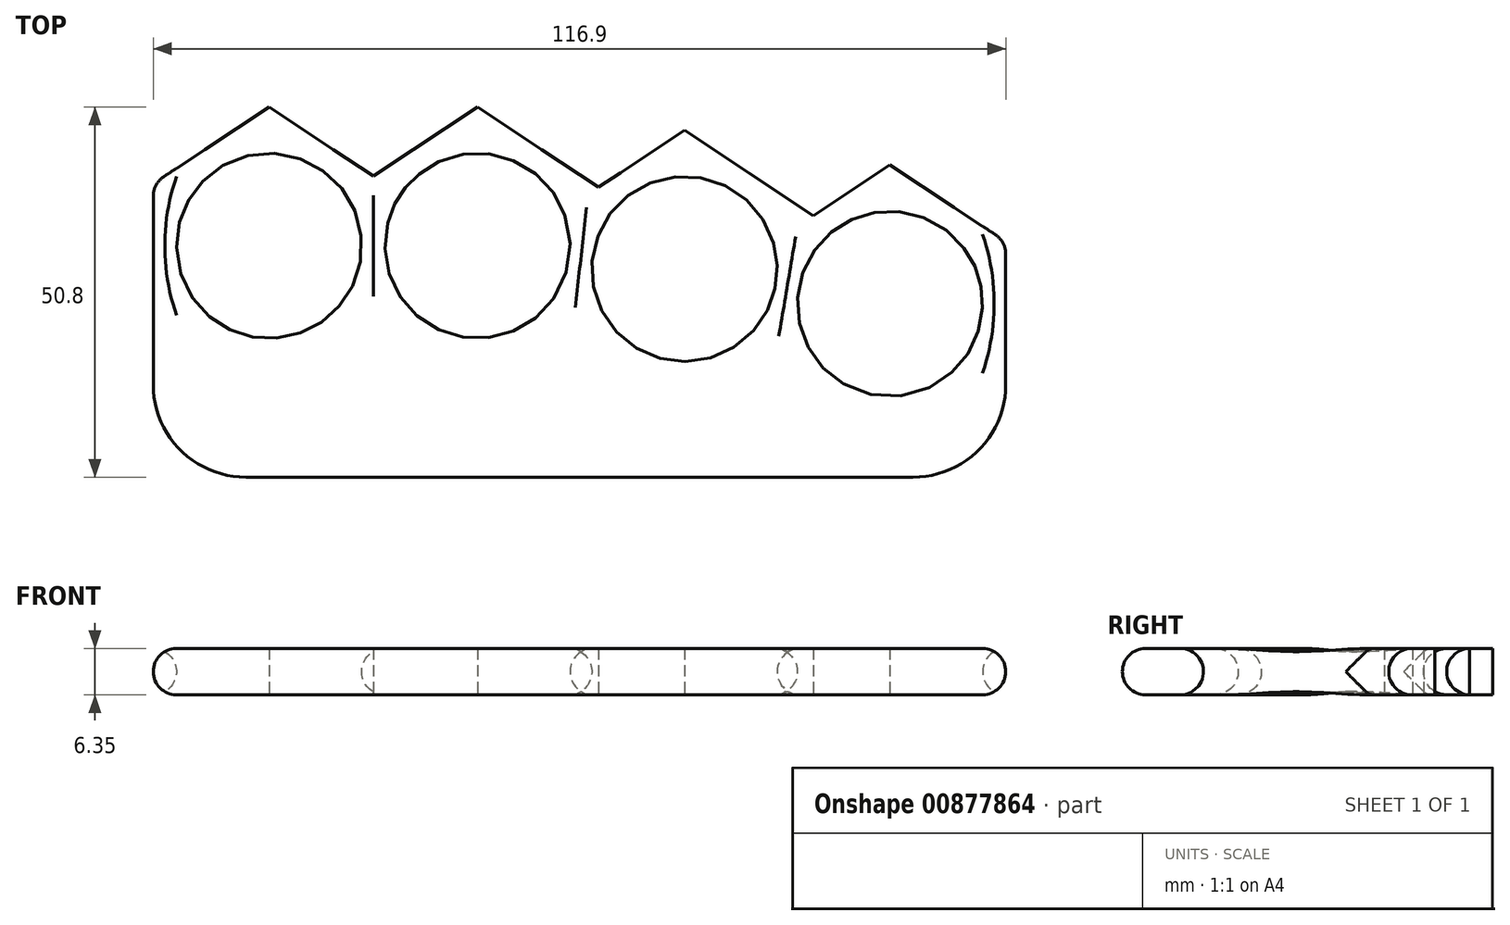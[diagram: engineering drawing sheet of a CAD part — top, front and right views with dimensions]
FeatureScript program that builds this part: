
annotation { "Feature Type Name" : "Feature", "Feature Type Description" : "" }
export const myFeature = defineFeature(function(context is Context, id is Id, definition is map)
    precondition{}
    {
        {
            var Q0;
            Q0=qCreatedBy(makeId("Top.planeOp"),FACE);
            var sketch = newSketch(context, id + "F0", { "sketchPlane" : qUnion([Q0])});
            skLineSegment(sketch, "E0.bottom", {"start": v(40.7, 0) * mm, "end": v(-50.8, 0) * mm});
            skLineSegment(sketch, "E0.top", {"start": v(63.5, 50.8) * mm, "end": v(-63.5, 50.8) * mm});
            skLineSegment(sketch, "E0.left", {"start": v(63.5, 0) * mm, "end": v(63.5, 50.8) * mm, "construction": true});
            skLineSegment(sketch, "E0.right", {"start": v(-63.5, 12.7) * mm, "end": v(-63.5, 50.8) * mm});
            skPoint(sketch, "E0.middle", {"position": v(0, 25.4) * mm});
            skLineSegment(sketch, "E1", {"start": v(-63.5, 19.05) * mm, "end": v(63.5, 19.05) * mm, "construction": true});
            skCircle(sketch, "E2", {"center": v(-19.05, 31.75) * mm, "radius": 12.7 * mm});
            skCircle(sketch, "E3", {"center": v(-47.62, 31.75) * mm, "radius": 12.7 * mm});
            skCircle(sketch, "E4", {"center": v(9.35, 28.58) * mm, "radius": 12.7 * mm});
            skCircle(sketch, "E5", {"center": v(37.52, 23.81) * mm, "radius": 12.7 * mm});
            skPoint(sketch, "E6.visualSharp", {"position": v(-63.5, 0) * mm});
            skArc(sketch, "E6.filletArc", {"start": v(-63.5, 12.7) * mm, "mid": v(-59.78, 3.72) * mm, "end": v(-50.8, 0) * mm});
            skLineSegment(sketch, "E7", {"start": v(-47.62, 50.8) * mm, "end": v(-63.5, 40.27) * mm});
            skLineSegment(sketch, "E8", {"start": v(-47.63, 50.8) * mm, "end": v(-33.34, 41.32) * mm});
            skLineSegment(sketch, "E9", {"start": v(-33.34, 41.32) * mm, "end": v(-19.05, 50.8) * mm});
            skLineSegment(sketch, "E10", {"start": v(-19.05, 50.8) * mm, "end": v(-2.46, 39.8) * mm});
            skPoint(sketch, "E11.start.orphan", {"position": v(9.35, 50.8) * mm});
            skPoint(sketch, "E12.end.orphan", {"position": v(37.52, 46.26) * mm});
            skPoint(sketch, "E13.start.orphan", {"position": v(59.97, 23.81) * mm});
            skLineSegment(sketch, "E14", {"start": v(-2.46, 39.8) * mm, "end": v(9.35, 47.63) * mm});
            skLineSegment(sketch, "E15", {"start": v(9.35, 47.63) * mm, "end": v(27.03, 35.9) * mm});
            skLineSegment(sketch, "E16", {"start": v(27.03, 35.9) * mm, "end": v(37.52, 42.86) * mm});
            skLineSegment(sketch, "E17", {"start": v(37.52, 42.86) * mm, "end": v(53.4, 32.33) * mm});
            skLineSegment(sketch, "E18", {"start": v(53.4, 32.33) * mm, "end": v(53.4, 12.7) * mm});
            skPoint(sketch, "E19.newPointA", {"position": v(53.4, 0) * mm});
            skPoint(sketch, "E19.newPointB", {"position": v(63.5, 0) * mm});
            skArc(sketch, "E19.filletArc", {"start": v(40.7, 0) * mm, "mid": v(49.68, 3.72) * mm, "end": v(53.4, 12.7) * mm});
            skSolve(sketch);
        }
        {
            var Q0;
            Q0=makeQuery(id+"F0.imprint","IMPRINT",FACE,{"disambiguationData":[TD([[makeQuery(id+"F0.imprint","IMPRINT",EDGE,{"derivedFrom":sQuery(id+"F0.wireOp",EDGE,"E2")}),-1.0]])]});
            extrude(context, id + "F1", {"entities" : qUnion([Q0]), "depth" : 6.35 * mm, "offsetDistance" : 25.4 * mm});
        }
        {
            var Q0;
            Q0=makeQuery(id+"F1.opExtrude","SWEPT_FACE",FACE,{"disambiguationData":[OSD([sQuery(id+"F0.wireOp",EDGE,"E3")])]});
            var Q1;
            Q1=makeQuery(id+"F1.opExtrude","SWEPT_FACE",FACE,{"disambiguationData":[OSD([sQuery(id+"F0.wireOp",EDGE,"E2")])]});
            var Q2;
            Q2=makeQuery(id+"F1.opExtrude","SWEPT_FACE",FACE,{"disambiguationData":[OSD([sQuery(id+"F0.wireOp",EDGE,"E4")])]});
            var Q3;
            Q3=makeQuery(id+"F1.opExtrude","SWEPT_FACE",FACE,{"disambiguationData":[OSD([sQuery(id+"F0.wireOp",EDGE,"E5")])]});
            var Q4;
            Q4=makeQuery(id+"F1.opExtrude","SWEPT_FACE",FACE,{"disambiguationData":[OSD([sQuery(id+"F0.wireOp",EDGE,"E0.bottom")])]});
            var Q5;
            Q5=makeQuery(id+"F1.opExtrude","SWEPT_FACE",FACE,{"disambiguationData":[OSD([sQuery(id+"F0.wireOp",EDGE,"E6.filletArc")])]});
            var Q6;
            Q6=makeQuery(id+"F1.opExtrude","SWEPT_FACE",FACE,{"disambiguationData":[OSD([sQuery(id+"F0.wireOp",EDGE,"E0.right")])]});
            var Q7;
            Q7=makeQuery(id+"F1.opExtrude","SWEPT_FACE",FACE,{"disambiguationData":[OSD([sQuery(id+"F0.wireOp",EDGE,"E18")])]});
            var Q8;
            Q8=makeQuery(id+"F1.opExtrude","SWEPT_FACE",FACE,{"disambiguationData":[OSD([sQuery(id+"F0.wireOp",EDGE,"E19.filletArc")])]});
            fillet(context, id + "F2", {"entities" : qUnion([Q0, Q1, Q2, Q3, Q4, Q5, Q6, Q7, Q8]), "radius" : 3.17 * mm, "allowEdgeOverflow" : false});
        }
    });
